# Revit family: 306_64c9dc49810b4e6eae7a94c1477eb5
name_source: partatom
category: Pipe Accessories
units: mm (PartAtom-declared; Revit-internal decimal feet)

## family parameters
Always vertical = Yes
Cut with Voids When Loaded = No
Part Type = Valve - Breaks Into
Round Connector Dimension = Use Diameter
Shared = No
Work Plane-Based = No

## types (7) — shared parameters
CAT0 = Yes
Description = 3-way Fan coil valve with by-pass VLG142, PN16 external thread
E = 16 mm  [stored 0.0524934 ft]
L2D = 38 mm  [stored 0.124672 ft]
L2D_Min = 3048 mm  [stored 10 ft]
MC = No
MC2 = Yes
Manufacturer = ESBE
QmdConnectorList = 301;D;302;D
R10 = 8 mm  [stored 0.0262467 ft]
R4 = 6 mm  [stored 0.019685 ft]
R5 = 7 mm  [stored 0.0229659 ft]
R7 = 15 mm  [stored 0.0492126 ft]
R8 = 2 mm  [stored 0.00656168 ft]
R9 = 9 mm  [stored 0.0295276 ft]
URL = http://www.esbe.eu
W2D = 15 mm  [stored 0.0492126 ft]
X4 = 7 mm  [stored 0.0229659 ft]
X4__ve = -7 mm  [stored -0.0229659 ft]
Z3 = 2 mm  [stored 0.00656168 ft]
Z5 = 9 mm  [stored 0.0295276 ft]
Z7 = 3 mm  [stored 0.00984252 ft]
Z7__ve = -3 mm
Z8 = 4 mm  [stored 0.0131234 ft]
magiPartTypeId = 306
magiProductFamilyId = 64c9dc49810b4e6eae7a94c1477eb5

## per-type parameters (varying)
| type | C | D | DT2 | H | H1 | LT2 | MC Product Code | R1 | R2 | R6 | X3 | Z2 | magiProductId |
| VLG142 PN16 15-0,25 G1/2 | 23 mm | 15 mm | 8 mm  [stored 0.0262467 ft] | 27 mm | 21 mm  [stored 0.0688976 ft] | 19 mm  [stored 0.062336 ft] | VLG142 PN16 15-0,25 G1/2" | 7 mm  [stored 0.0229659 ft] | 13 mm | 11 mm | 34 mm | 8 mm  [stored 0.0262467 ft] | 03c722ae10144acd9300c77907ef5a |
| VLG142 PN16 15-0,4 G1/2 | 23 mm | 15 mm | 8 mm  [stored 0.0262467 ft] | 27 mm | 21 mm  [stored 0.0688976 ft] | 19 mm  [stored 0.062336 ft] | VLG142 PN16 15-0,4 G1/2" | 7 mm  [stored 0.0229659 ft] | 13 mm | 11 mm | 34 mm | 8 mm  [stored 0.0262467 ft] | d7562f636cca42bca33492f2c72c6c |
| VLG142 PN16 15-1,0 G1/2 | 23 mm | 15 mm | 8 mm  [stored 0.0262467 ft] | 27 mm | 21 mm  [stored 0.0688976 ft] | 19 mm  [stored 0.062336 ft] | VLG142 PN16 15-1,0 G1/2" | 7 mm  [stored 0.0229659 ft] | 13 mm | 11 mm | 34 mm | 8 mm  [stored 0.0262467 ft] | 53dc8ab558694086971e08e89fcdde |
| VLG142 PN16 15-1,6 G1/2 | 23 mm | 15 mm | 8 mm  [stored 0.0262467 ft] | 27 mm | 21 mm  [stored 0.0688976 ft] | 19 mm  [stored 0.062336 ft] | VLG142 PN16 15-1,6 G1/2" | 7 mm  [stored 0.0229659 ft] | 13 mm | 11 mm | 34 mm | 8 mm  [stored 0.0262467 ft] | 7299051495c3495b99a2e309be1569 |
| VLG142 PN16 20-2,5 G3/4 | 50 mm  [stored 0.164042 ft] | 20 mm | 10 mm  [stored 0.0328084 ft] | 26 mm  [stored 0.0853018 ft] | 37 mm | 21 mm  [stored 0.0688976 ft] | VLG142 PN16 20-2,5 G3/4" | 9 mm  [stored 0.0295276 ft] | 15 mm  [stored 0.0492126 ft] | 12 mm  [stored 0.0393701 ft] | 38 mm  [stored 0.124672 ft] | 18 mm  [stored 0.0590551 ft] | 7f6e62aac6e449fea771c4bc16d675 |
| VLG142 PN16 20-4,0 G3/4 | 50 mm  [stored 0.164042 ft] | 20 mm | 10 mm  [stored 0.0328084 ft] | 26 mm  [stored 0.0853018 ft] | 37 mm | 21 mm  [stored 0.0688976 ft] | VLG142 PN16 20-4,0 G3/4" | 9 mm  [stored 0.0295276 ft] | 15 mm  [stored 0.0492126 ft] | 12 mm  [stored 0.0393701 ft] | 38 mm  [stored 0.124672 ft] | 18 mm  [stored 0.0590551 ft] | 042013fa93394101928eff02912b96 |
| VLG142 PN16 20-6,0 G3/4 | 50 mm  [stored 0.164042 ft] | 20 mm | 10 mm  [stored 0.0328084 ft] | 26 mm  [stored 0.0853018 ft] | 37 mm | 21 mm  [stored 0.0688976 ft] | VLG142 PN16 20-6,0 G3/4" | 9 mm  [stored 0.0295276 ft] | 15 mm  [stored 0.0492126 ft] | 12 mm  [stored 0.0393701 ft] | 38 mm  [stored 0.124672 ft] | 18 mm  [stored 0.0590551 ft] | c21606ec393c49548766728e14367f |

note: [stored X ft] marks values corroborated as IEEE doubles in the binary element streams (Revit-internal decimal feet)

## geometry (parser evidence)
native form markers: Sweep x2
no freeform markers — native parametric forms only
